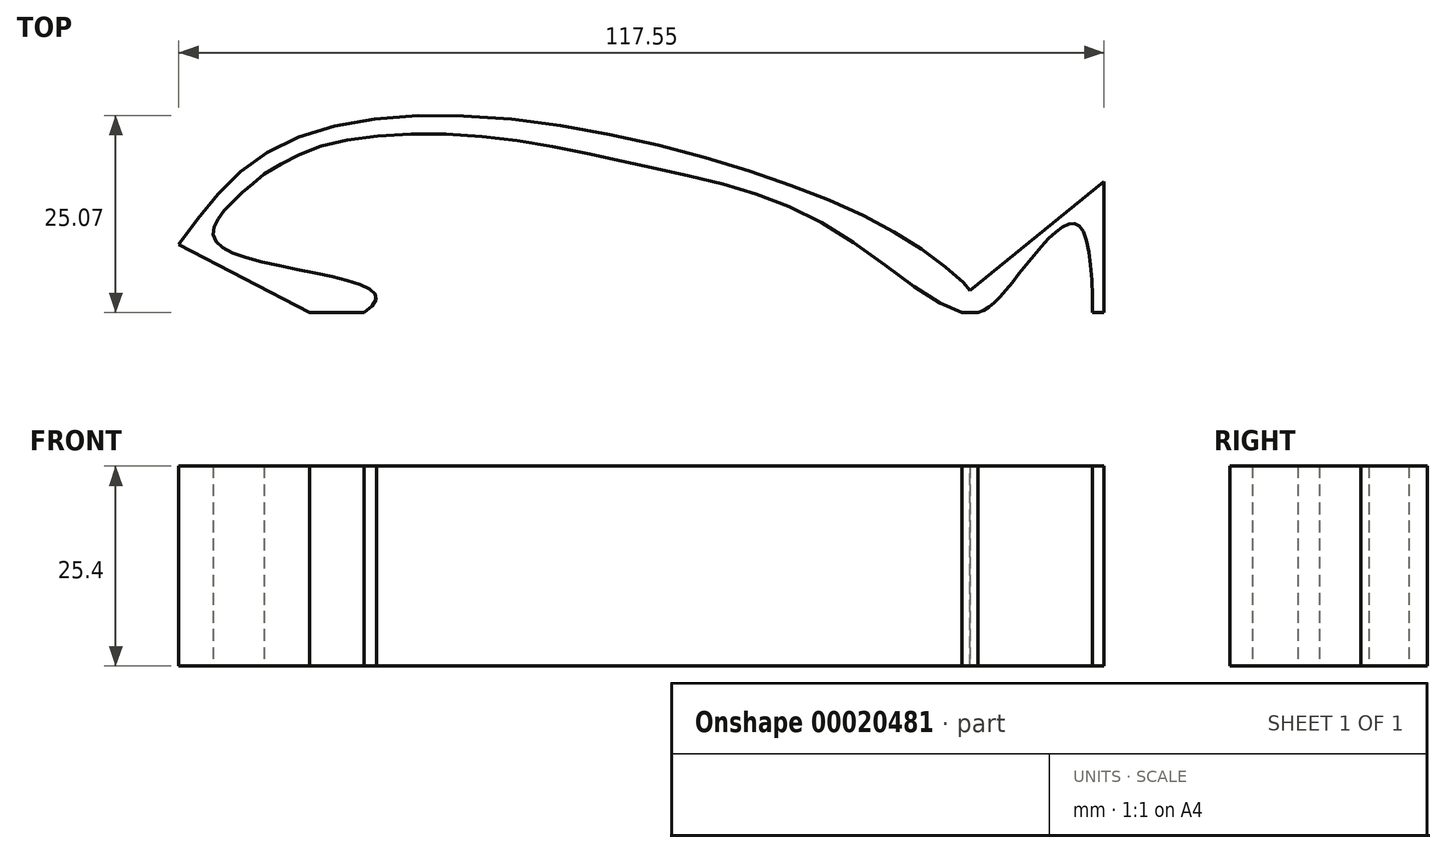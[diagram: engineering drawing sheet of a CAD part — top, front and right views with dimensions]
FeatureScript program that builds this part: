
annotation { "Feature Type Name" : "Feature", "Feature Type Description" : "" }
export const myFeature = defineFeature(function(context is Context, id is Id, definition is map)
    precondition{}
    {
        {
            var Q0;
            Q0=qCreatedBy(makeId("Top.planeOp"),FACE);
            var sketch = newSketch(context, id + "F0", { "sketchPlane" : qUnion([Q0])});
            skFitSpline(sketch, "E0", {"points": [v(-56.07, 24.85) * mm, v(-44.19, 36.95) * mm, v(-16.96, 41.06) * mm, v(20.42, 32.84) * mm, v(39.65, 23.34) * mm, v(44.4, 19.02) * mm, v(44.19, 19.02) * mm], "startDerivative": vector(56.06, 77.3) * mm, "endDerivative": vector(-14.67, 3.18) * mm});
            skLineSegment(sketch, "E1", {"start": v(-76.38, 16.2) * mm, "end": v(76.6, 16.2) * mm});
            skFitSpline(sketch, "E2.MirrorCS", {"points": [v(-56.07, 7.56) * mm, v(-44.19, -4.54) * mm, v(-16.96, -8.64) * mm, v(20.42, -0.43) * mm, v(39.65, 9.08) * mm, v(44.4, 13.4) * mm, v(44.19, 13.4) * mm], "startDerivative": vector(56.06, -77.3) * mm, "endDerivative": vector(-14.67, -3.18) * mm});
            skLineSegment(sketch, "E3", {"start": v(-56.07, 7.56) * mm, "end": v(-39.43, 16.2) * mm});
            skLineSegment(sketch, "E4", {"start": v(-39.43, 16.2) * mm, "end": v(-56.07, 24.85) * mm});
            skLineSegment(sketch, "E5", {"start": v(44.4, 19.02) * mm, "end": v(61.48, 32.84) * mm});
            skLineSegment(sketch, "E6", {"start": v(44.4, 13.4) * mm, "end": v(61.48, 0) * mm});
            skLineSegment(sketch, "E7", {"start": v(61.48, 0) * mm, "end": v(61.48, 32.84) * mm});
            skCircle(sketch, "E8", {"center": v(-35.98, 28.95) * mm, "radius": 4.51 * mm});
            skFitSpline(sketch, "E9", {"points": [v(-45.2, 33.83) * mm, v(-37.68, 37.45) * mm, v(-18.35, 38.66) * mm, v(4.6, 34.5) * mm, v(26.08, 27.39) * mm, v(43.4, 16.2) * mm, v(49.44, 19.6) * mm, v(58.44, 27.12) * mm, v(59.91, 4.03) * mm, v(60.05, 4.03) * mm], "startDerivative": vector(73.15, 45.84) * mm, "endDerivative": vector(13.1, 9.44) * mm});
            skFitSpline(sketch, "E10", {"points": [v(60.05, 4.03) * mm, v(44.4, 14.77) * mm, v(23.4, 4.03) * mm, v(1.52, -3.09) * mm, v(-19.02, -5.5) * mm, v(-39.7, -2.95) * mm, v(-49.63, 5.37) * mm, v(-30.97, 18.26) * mm, v(-50.97, 24.85) * mm, v(-45.2, 33.83) * mm], "startDerivative": vector(-134.59, 145.2) * mm, "endDerivative": vector(147.75, 122.78) * mm});
            skSolve(sketch);
        }
        {
            var Q0;
            {var subQ9=sQuery(id+"F0.wireOp",EDGE,"E4");Q0=makeQuery(id+"F0.imprint","IMPRINT",FACE,{"disambiguationData":[TD([[makeQuery(id+"F0.imprint","IMPRINT",EDGE,{"derivedFrom":subQ9}),-1.0]])]});}
            extrude(context, id + "F1", {"entities" : qUnion([Q0]), "depth" : 25.4 * mm});
        }
    });
